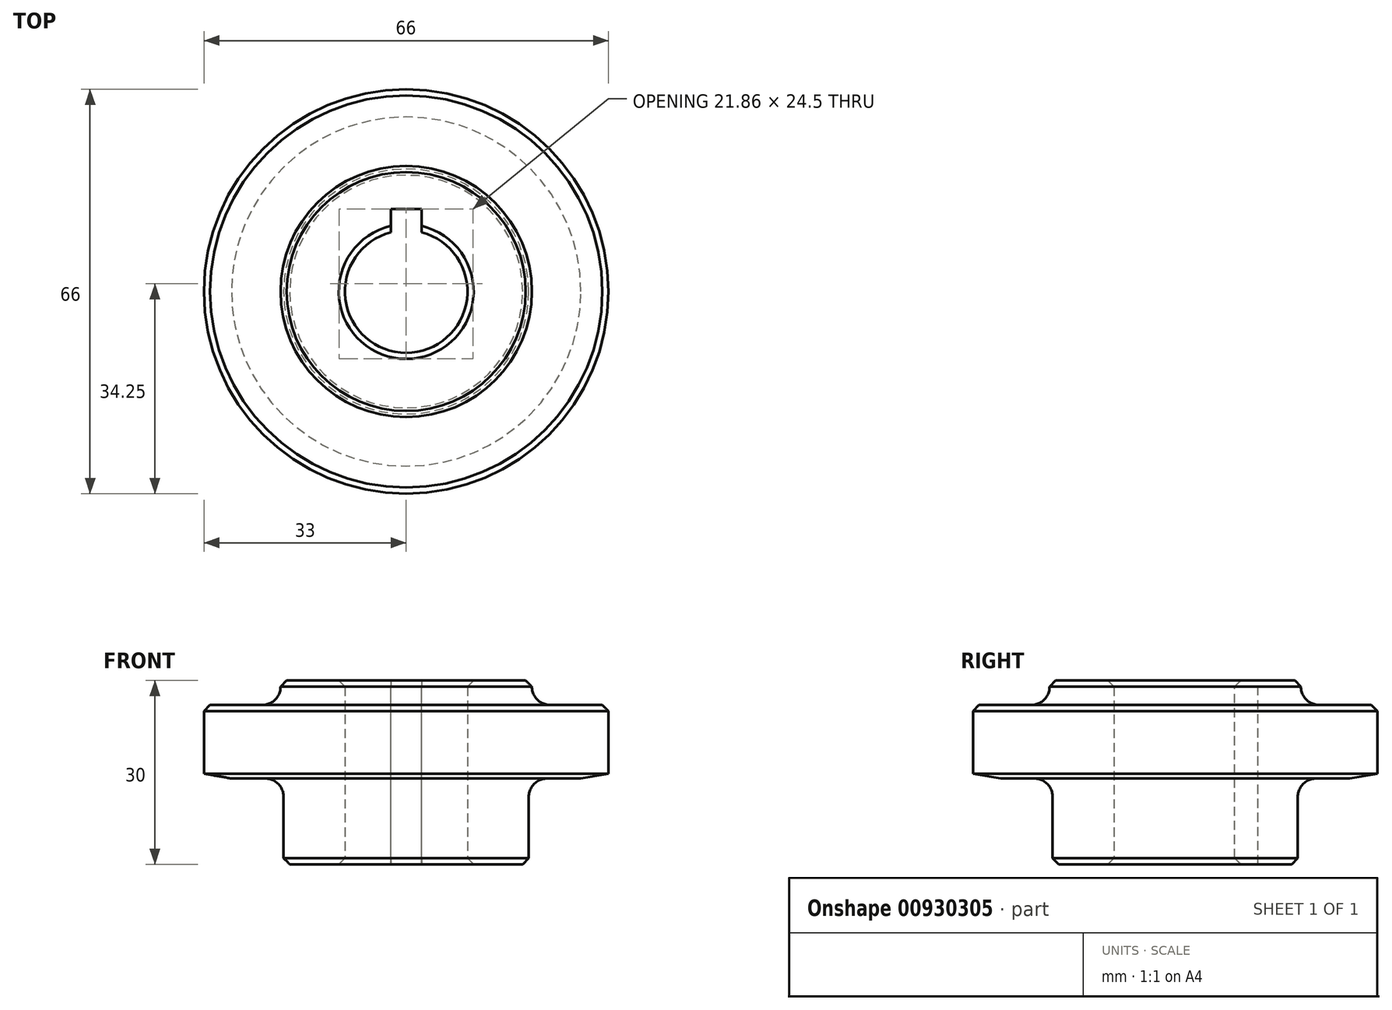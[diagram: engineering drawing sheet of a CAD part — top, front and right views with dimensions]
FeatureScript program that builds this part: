
annotation { "Feature Type Name" : "Feature", "Feature Type Description" : "" }
export const myFeature = defineFeature(function(context is Context, id is Id, definition is map)
    precondition{}
    {
        {
            var Q0;
            Q0=qCreatedBy(makeId("Front.planeOp"),FACE);
            var sketch = newSketch(context, id + "F0", { "sketchPlane" : qUnion([Q0])});
            skLineSegment(sketch, "E0", {"start": v(10, 0) * mm, "end": v(20, 0) * mm});
            skLineSegment(sketch, "E1", {"start": v(20, 0) * mm, "end": v(20, 14) * mm});
            skLineSegment(sketch, "E2", {"start": v(20, 14) * mm, "end": v(28.5, 14) * mm});
            skLineSegment(sketch, "E3", {"start": v(28.5, 14) * mm, "end": v(33, 14.8) * mm});
            skLineSegment(sketch, "E4", {"start": v(33, 14.8) * mm, "end": v(33, 26) * mm});
            skLineSegment(sketch, "E5", {"start": v(33, 26) * mm, "end": v(20.5, 26) * mm});
            skLineSegment(sketch, "E6", {"start": v(20.5, 26) * mm, "end": v(20.5, 30) * mm});
            skLineSegment(sketch, "E7", {"start": v(20.5, 30) * mm, "end": v(10, 30) * mm});
            skLineSegment(sketch, "E8.0", {"start": v(10, 30) * mm, "end": v(10, 0) * mm});
            skLineSegment(sketch, "E9", {"start": v(0, 0) * mm, "end": v(0, 5.88) * mm});
            skSolve(sketch);
        }
        {
            var Q0;
            Q0=makeQuery(id+"F0.imprint","IMPRINT",FACE,{"disambiguationData":[TD([[makeQuery(id+"F0.imprint","IMPRINT",EDGE,{"derivedFrom":sQuery(id+"F0.wireOp",EDGE,"E0")}),1.0]])]});
            var Q1;
            Q1=sQuery(id+"F0.wireOp",EDGE,"E9");
            revolve(context, id + "F1", {"surfaceOperationType" : NewSurfaceOperationType.NEW, "entities" : qUnion([Q0]), "axis" : qUnion([Q1]), "revolveType" : RevolveType.FULL});
        }
        {
            var Q0;
            Q0=makeQuery(id+"F1.opRevolve","SWEPT_EDGE",EDGE,{"disambiguationData":[OSD([sQuery(id+"F0.wireOp",EDGE,"E6"),sQuery(id+"F0.wireOp",EDGE,"E7")])]});
            var Q1;
            Q1=makeQuery(id+"F1.opRevolve","SWEPT_EDGE",EDGE,{"disambiguationData":[OSD([sQuery(id+"F0.wireOp",EDGE,"E4"),sQuery(id+"F0.wireOp",EDGE,"E5")])]});
            var Q2;
            Q2=makeQuery(id+"F1.opRevolve","SWEPT_EDGE",EDGE,{"disambiguationData":[OSD([sQuery(id+"F0.wireOp",EDGE,"E0"),sQuery(id+"F0.wireOp",EDGE,"E1")])]});
            var Q3;
            Q3=makeQuery(id+"F1.opRevolve","SWEPT_EDGE",EDGE,{"disambiguationData":[OSD([sQuery(id+"F0.wireOp",EDGE,"E7"),sQuery(id+"F0.wireOp",EDGE,"E8.0")])]});
            var Q4;
            Q4=makeQuery(id+"F1.opRevolve","SWEPT_EDGE",EDGE,{"disambiguationData":[OSD([sQuery(id+"F0.wireOp",EDGE,"E0"),sQuery(id+"F0.wireOp",EDGE,"E8.0")])]});
            chamfer(context, id + "F2", {"entities" : qUnion([Q0, Q1, Q2, Q3, Q4]), "width" : 1 * mm, "tangentPropagation" : true});
        }
        {
            var Q0;
            Q0=makeQuery(id+"F1.opRevolve","SWEPT_EDGE",EDGE,{"disambiguationData":[OSD([sQuery(id+"F0.wireOp",EDGE,"E1"),sQuery(id+"F0.wireOp",EDGE,"E2")])]});
            var Q1;
            Q1=makeQuery(id+"F1.opRevolve","SWEPT_EDGE",EDGE,{"disambiguationData":[OSD([sQuery(id+"F0.wireOp",EDGE,"E5"),sQuery(id+"F0.wireOp",EDGE,"E6")])]});
            fillet(context, id + "F3", {"entities" : qUnion([Q0, Q1]), "tangentPropagation" : true, "radius" : 3 * mm, "defaultsChanged" : false, "vertexSettings" : [], "allowEdgeOverflow" : false});
        }
        {
            var Q0;
            Q0=makeQuery(id+"F1.opRevolve","SWEPT_FACE",FACE,{"disambiguationData":[OSD([sQuery(id+"F0.wireOp",EDGE,"E7")])]});
            var sketch = newSketch(context, id + "F4", { "sketchPlane" : qUnion([Q0])});
            skLineSegment(sketch, "E10", {"start": v(-2.5, 13.5) * mm, "end": v(2.5, 13.5) * mm});
            skLineSegment(sketch, "E11", {"start": v(-2.5, 13.5) * mm, "end": v(-2.5, 9.68) * mm});
            skLineSegment(sketch, "E12", {"start": v(2.5, 13.5) * mm, "end": v(2.5, 9.68) * mm});
            skArc(sketch, "E13.0", {"start": v(2.5, 9.68) * mm, "mid": v(0, 10) * mm, "end": v(-2.5, 9.68) * mm});
            skSolve(sketch);
        }
        {
            var Q0;
            {var subQ0=sQuery(id+"F4.wireOp",EDGE,"E10");Q0=makeQuery(id+"F4.imprint","IMPRINT",FACE,{"disambiguationData":[TD([[makeQuery(id+"F4.imprint","IMPRINT",EDGE,{"derivedFrom":subQ0}),-1.0]])]});}
            var Q1;
            {var subQ0=sQuery(id+"F4.wireOp",EDGE,"E13.0");Q1=makeQuery(id+"F4.imprint","IMPRINT",FACE,{"disambiguationData":[TD([[makeQuery(id+"F4.imprint","IMPRINT",EDGE,{"derivedFrom":subQ0}),-1.0]])]});}
            var Q2;
            Q2=makeQuery(id+"F1.opRevolve","SWEPT_FACE",FACE,{"disambiguationData":[OSD([sQuery(id+"F0.wireOp",EDGE,"E0")])]});
            extrude(context, id + "F5", {"entities" : qUnion([Q0, Q1]), "operationType" : NewBodyOperationType.REMOVE, "endBound" : BoundingType.UP_TO_SURFACE, "oppositeDirection" : true, "depth" : 25 * mm, "endBoundEntityFace" : qUnion([Q2]), "offsetDistance" : 25 * mm});
        }
    });
